# Revit family: M-Miscellaneous Wide Flange-Column
name_source: partatom
category: Structural Columns
revit_build: Autodesk Revit Architecture 2012 (Build: 20110210_1515)
units: mm (PartAtom-declared; Revit-internal decimal feet)

## types (18) — shared parameters
Assembly Code = B10

## per-type parameters (varying)
| type | A | W | bf | d | k | kr | tf | tw |
| M12.5X12.4 | 3.63 in² | 12.4 | 0' - 3 3/4" | 1' - 0 1/2" | 0' - 0 9/16" | 0' - 0 5/16" | 0' - 0 1/4" | 0' - 0 1/8" |
| M12.5X11.6 | 3.4 in² | 11.6 | 0' - 3 1/2" | 1' - 0 1/2" | 0' - 0 9/16" | 0' - 0 3/8" | 0' - 0 3/16" | 0' - 0 1/8" |
| M12X11.8 | 3.47 in² | 11.8 | 0' - 3 1/16" | 1' - 0" | 0' - 0 9/16" | 0' - 0 5/16" | 0' - 0 1/4" | 0' - 0 3/16" |
| M12X10.8 | 3.18 in² | 10.8 | 0' - 3 1/16" | 1' - 0" | 0' - 0 9/16" | 0' - 0 3/8" | 0' - 0 3/16" | 0' - 0 3/16" |
| M12X10 | 2.95 in² | 10 | 0' - 3 1/4" | 1' - 0" | 0' - 0 1/2" | 0' - 0 5/16" | 0' - 0 3/16" | 0' - 0 1/8" |
| M10X9 | 2.65 in² | 9 | 0' - 2 11/16" | 0' - 10" | 0' - 0 9/16" | 0' - 0 3/8" | 0' - 0 3/16" | 0' - 0 3/16" |
| M10X8 | 2.37 in² | 8 | 0' - 2 11/16" | 0' - 10" | 0' - 0 9/16" | 0' - 0 3/8" | 0' - 0 3/16" | 0' - 0 1/8" |
| M10X7.5 | 2.22 in² | 7.5 | 0' - 2 11/16" | 0' - 10" | 0' - 0 7/16" | 0' - 0 1/4" | 0' - 0 3/16" | 0' - 0 1/8" |
| M8X6.5 | 1.92 in² | 6.5 | 0' - 2 1/4" | 0' - 8" | 0' - 0 9/16" | 0' - 0 3/8" | 0' - 0 3/16" | 0' - 0 1/8" |
| M8X6.2 | 1.82 in² | 6.2 | 0' - 2 1/4" | 0' - 8" | 0' - 0 7/16" | 0' - 0 1/4" | 0' - 0 3/16" | 0' - 0 1/8" |
| M6X4.4 | 1.29 in² | 4.4 | 0' - 1 13/16" | 0' - 6" | 0' - 0 3/8" | 0' - 0 3/16" | 0' - 0 3/16" | 0' - 0 1/8" |
| M6X3.7 | 1.09 in² | 3.7 | 0' - 2" | 0' - 5 15/16" | 0' - 0 5/16" | 0' - 0 3/16" | 0' - 0 1/8" | 0' - 0 1/8" |
| M5X18.9 | 5.56 in² | 18.9 | 0' - 5" | 0' - 5" | 0' - 0 13/16" | 0' - 0 3/8" | 0' - 0 7/16" | 0' - 0 5/16" |
| M4X6 | 1.75 in² | 6 | 0' - 3 13/16" | 0' - 3 13/16" | 0' - 0 1/2" | 0' - 0 5/16" | 0' - 0 3/16" | 0' - 0 1/8" |
| M4X4.08 | 1.27 in² | 4.09 | 0' - 2 1/4" | 0' - 4" | 0' - 0 9/16" | 0' - 0 3/8" | 0' - 0 3/16" | 0' - 0 1/8" |
| M4X3.45 | 1.01 in² | 3.45 | 0' - 2 1/4" | 0' - 4" | 0' - 0 1/2" | 0' - 0 3/8" | 0' - 0 1/8" | 0' - 0 1/16" |
| M4X3.2 | 1.01 in² | 3.2 | 0' - 2 1/4" | 0' - 4" | 0' - 0 1/2" | 0' - 0 3/8" | 0' - 0 1/8" | 0' - 0 1/16" |
| M3X2.9 | 0.91 in² | 2.9 | 0' - 2 1/4" | 0' - 3" | 0' - 0 1/2" | 0' - 0 3/8" | 0' - 0 1/8" | 0' - 0 1/16" |

## geometry (parser evidence)
native form markers: Sweep x1
no freeform markers — native parametric forms only
